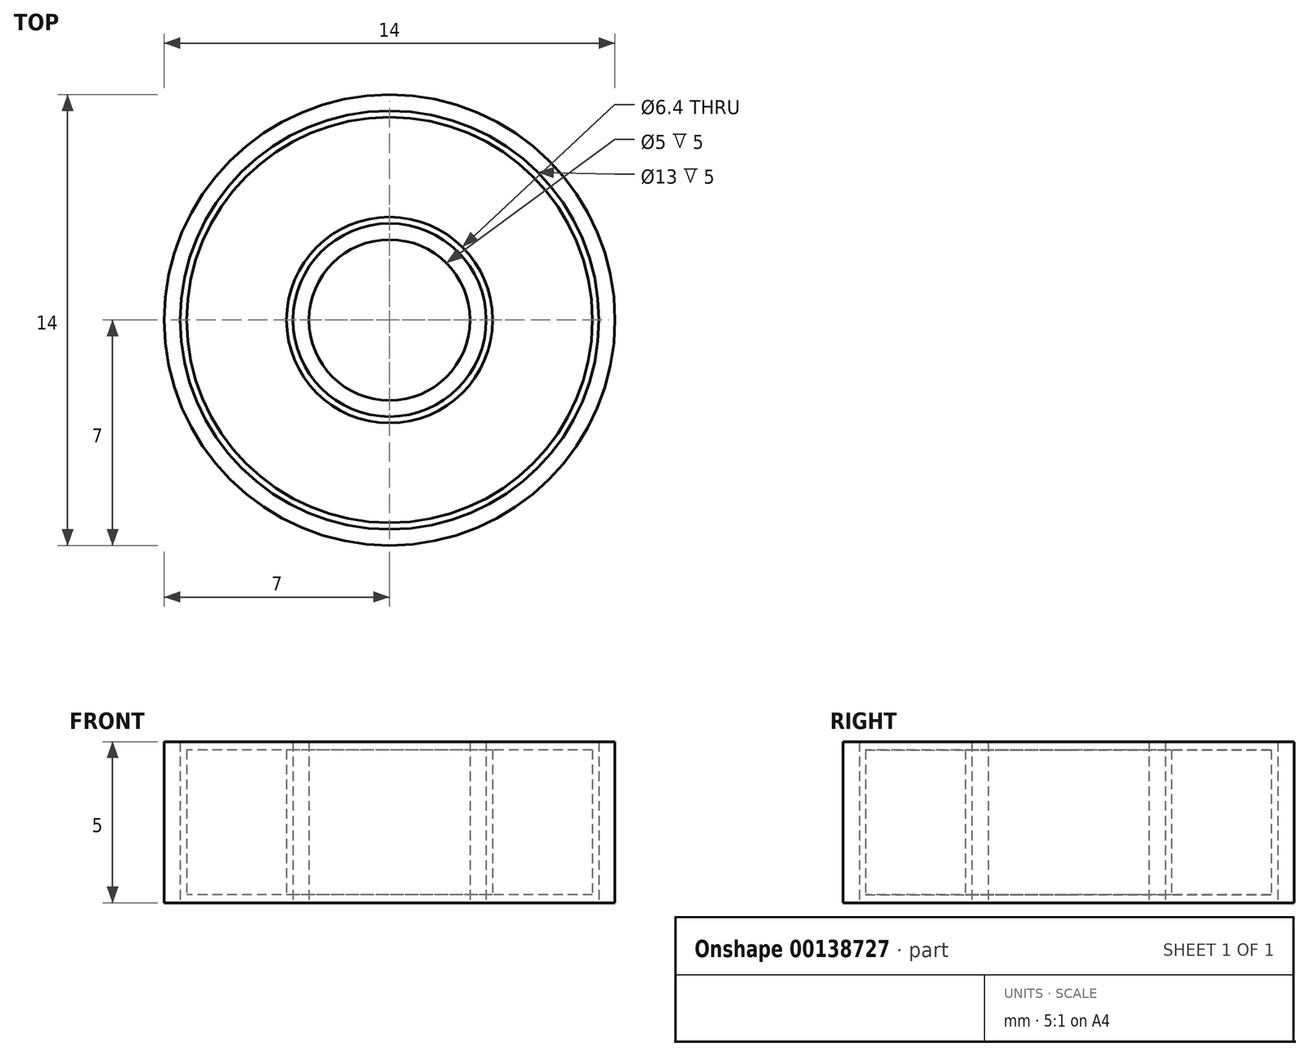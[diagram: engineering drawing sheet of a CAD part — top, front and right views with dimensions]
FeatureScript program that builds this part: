
annotation { "Feature Type Name" : "Feature", "Feature Type Description" : "" }
export const myFeature = defineFeature(function(context is Context, id is Id, definition is map)
    precondition{}
    {
        {
            var Q0;
            Q0=qCreatedBy(makeId("Top.planeOp"),FACE);
            var sketch = newSketch(context, id + "F0", { "sketchPlane" : qUnion([Q0])});
            skCircle(sketch, "E0", {"center": v(0, 0) * mm, "radius": 2.5 * mm});
            skCircle(sketch, "E1", {"center": v(0, 0) * mm, "radius": 3 * mm});
            skCircle(sketch, "E2", {"center": v(0, 0) * mm, "radius": 7 * mm});
            skCircle(sketch, "E3", {"center": v(0, 0) * mm, "radius": 6.5 * mm});
            skSolve(sketch);
        }
        {
            var Q0;
            Q0=makeQuery(id+"F0.imprint","IMPRINT",FACE,{"disambiguationData":[TD([[makeQuery(id+"F0.imprint","IMPRINT",EDGE,{"derivedFrom":sQuery(id+"F0.wireOp",EDGE,"E2")}),1.0]])]});
            var Q1;
            Q1=makeQuery(id+"F0.imprint","IMPRINT",FACE,{"disambiguationData":[TD([[makeQuery(id+"F0.imprint","IMPRINT",EDGE,{"derivedFrom":sQuery(id+"F0.wireOp",EDGE,"E0")}),-1.0]])]});
            extrude(context, id + "F1", {"entities" : qUnion([Q0, Q1]), "depth" : 5 * mm});
        }
        {
            var Q0;
            Q0=qCreatedBy(makeId("Top.planeOp"),FACE);
            var sketch = newSketch(context, id + "F2", { "sketchPlane" : qUnion([Q0])});
            skCircle(sketch, "E4", {"center": v(0, 0) * mm, "radius": 3.2 * mm});
            skCircle(sketch, "E5", {"center": v(0, 0) * mm, "radius": 6.3 * mm});
            skSolve(sketch);
        }
        {
            var Q0;
            Q0=makeQuery(id+"F2.imprint","IMPRINT",FACE,{"disambiguationData":[TD([[makeQuery(id+"F2.imprint","IMPRINT",EDGE,{"derivedFrom":sQuery(id+"F2.wireOp",EDGE,"E4")}),-1.0]])]});
            extrude(context, id + "F3", {"entities" : qUnion([Q0]), "depth" : 4.5 * mm});
        }
        {
            var Q0;
            Q0=makeQuery(id+"F3.opExtrude","SWEPT_BODY",BODY,{"disambiguationData":[OSD([sQuery(id+"F2.wireOp",EDGE,"E4"),sQuery(id+"F2.wireOp",EDGE,"E5")])]});
            transform(context, id + "F4", {"entities" : qUnion([Q0]), "transformType" : TransformType.TRANSLATION_3D, "dx" : 0 * mm, "dy" : 0 * mm, "dz" : 0.25 * mm, "makeCopy" : false});
        }
    });
